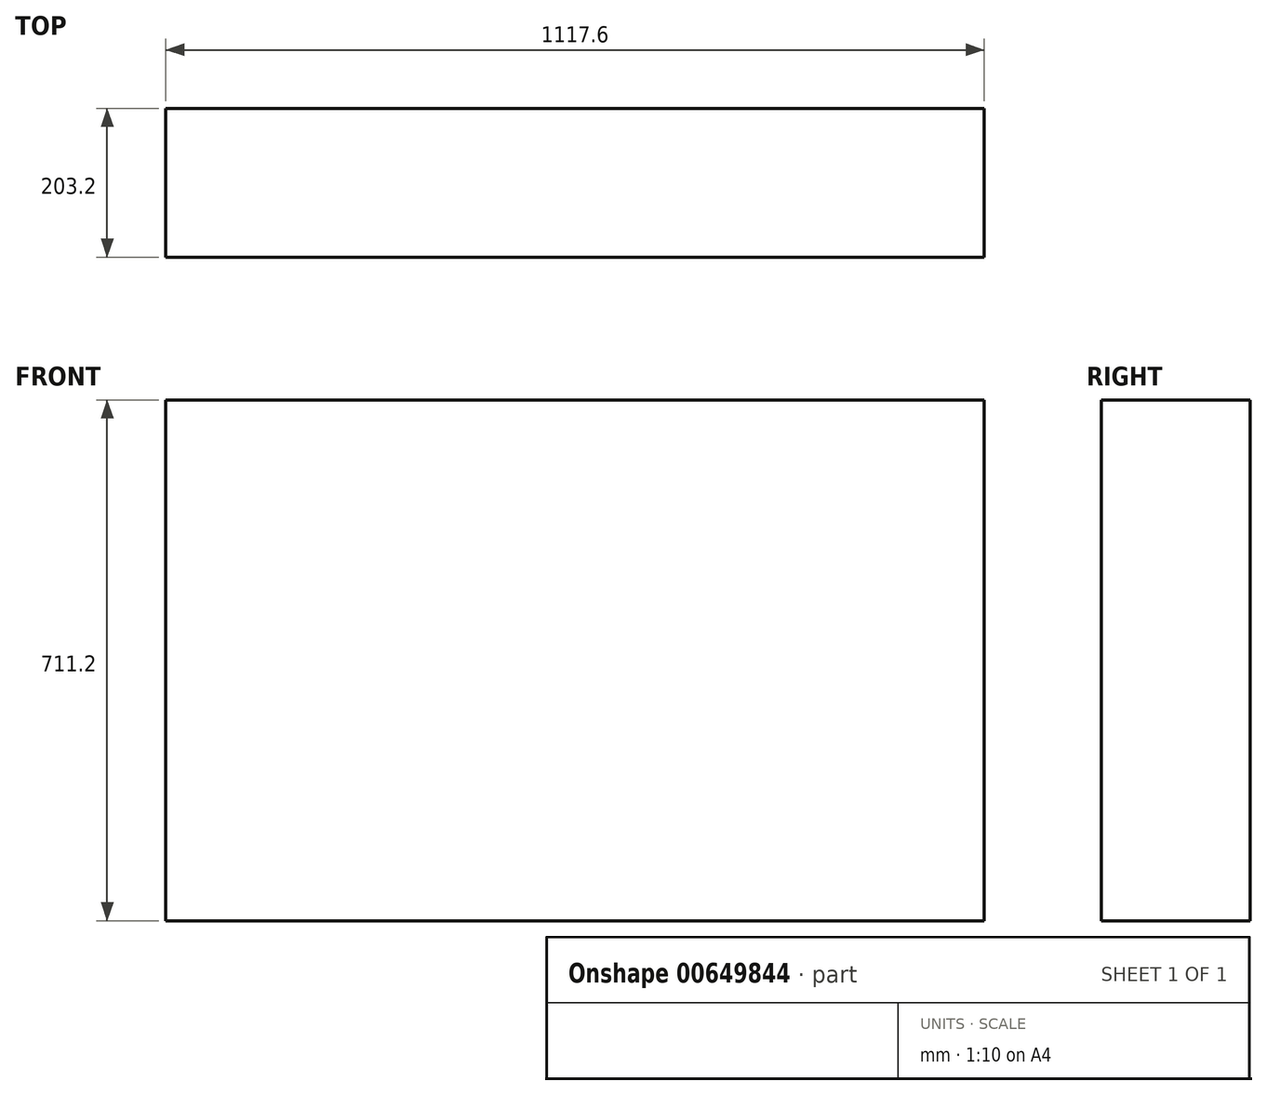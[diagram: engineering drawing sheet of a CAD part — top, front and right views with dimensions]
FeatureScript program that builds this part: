
annotation { "Feature Type Name" : "Feature", "Feature Type Description" : "" }
export const myFeature = defineFeature(function(context is Context, id is Id, definition is map)
    precondition{}
    {
        {
            var Q0;
            Q0=qCreatedBy(makeId("Front.planeOp"),FACE);
            var sketch = newSketch(context, id + "F0", { "sketchPlane" : qUnion([Q0])});
            skLineSegment(sketch, "E0.bottom", {"start": v(-552.47, 434.6) * mm, "end": v(565.13, 434.6) * mm});
            skLineSegment(sketch, "E0.top", {"start": v(-552.47, -276.6) * mm, "end": v(565.13, -276.6) * mm});
            skLineSegment(sketch, "E0.left", {"start": v(-552.47, 434.6) * mm, "end": v(-552.47, -276.6) * mm});
            skLineSegment(sketch, "E0.right", {"start": v(565.13, 434.6) * mm, "end": v(565.13, -276.6) * mm});
            skSolve(sketch);
        }
        {
            var Q0;
            Q0 = qSketchRegion(id + "F0", true);
            extrude(context, id + "F1", {"entities" : qUnion([Q0]), "depth" : 203.2 * mm, "offsetDistance" : 25.4 * mm});
        }
    });
